# Revit family: HoneyWell-RP1r-Supra-VSN-RP1r-ESS-RP1r-Supra
name_source: partatom
category: Electrical Equipment
revit_build: Autodesk Revit 2013 (Build: 20120221_2030(x64)
units: mm (PartAtom-declared; Revit-internal decimal feet)

## types (3) — shared parameters
AmbientClass = A-Class
ApparentLoad = 65 VA
Assembly Code = D5030700
Batteries = 2 x (12V-7Ah)
BatteryResistivity = 0.0700 ohm·m
COMDigitalInput = 1xNA/NC Config Digital Input
COMPorts = 2xRS-232; 1x ICseries; 1xUSB
CPD-Certification = 1134-CPD-045
CharguerCurrent = 300.0 mA
Depth = 123 mm  [stored 0.403543 ft]
Description = Extinguishing Control Panel
DigitalInput = Yes
ElectricClassification = Class 1 (Earthing required)
EmergencySupply = 24 V
FPAuxiliaryInputsContacts = 2x Manual release call points; 1x Hold device connection; 1x Abort emergency connection; 3x Technical alarm contacts
FPAuxiliaryRelayOutputs = 1x General fault relay; 3x Release status relays; 3x Operating mode relays
FPBuzzer = SPL min = 60dBA at 1m
FPDetection Zones = 2x Convencional detectors; 1x Configurable zone for detector or manual call point
FPReleaseCircuits = 2x Monitored output circuits for extinguishing (2 x 1A)
FPSounderCircuits = 2x Monitored output circuits for sounders (2 x 250mA)
Frequency (Hz) = 50/60 Hz
Height = 353 mm  [stored 1.15814 ft]
Homologation = UNE-EN 12094-1:2004, UNE-EN 54-2 y UNE-EN 54-4/A2:2006
IPRating = IP30
ITAC = Yes
InternalClock = RTC (CR2016/CR2025/CR2032) - 1000 Events Record
MainPowerFuse = T4AL-250V (4A)
Manufacturer = Honeywell
MaxElectricalCurrent = 28Vdc ±100 mV
MaxPower(EmergencySupply) = 2.4A (65W)
OPC-RP1r = Yes
OperationTemperature(Interior) = -5ºC to -40ºC
OutputLoads = máx. 1 A @ 30 Vdc
PowerFactor = 1
RelativeHumidity(RH) = 95% max
StandByConsumption = 125.0 mA
TG-IP-1 = Yes
TG-RP1r = Yes
UCIP = Yes
URL = https://www.notifier.es
VSN-232 = Yes
VSN-4REL = Yes
Voltage = 230
Wattage = 65
Weight(Batteries) = 9.3
Weight(NoBatteries) = 4
Width = 381 mm  [stored 1.25 ft]

## per-type parameters (varying)
| type | BoxMaterial | Connector(V) | PanelMaterial | TactileDisplay |
| RP1r-Supra | Steel,Black | 230/115 V | Steel,Black | Yes |
| VSN-RP1r+ | <By Category> | 115/230 V | <By Category> | No |
| ESS-RP1r-Supra | Steel,Black | 115/230 V | Steel,Black | Yes |

note: column(s) folded — value = type name in every type: Model

note: [stored X ft] marks values corroborated as IEEE doubles in the binary element streams (Revit-internal decimal feet)

## geometry (parser evidence)
native form markers: Sweep x2
no freeform markers — native parametric forms only
